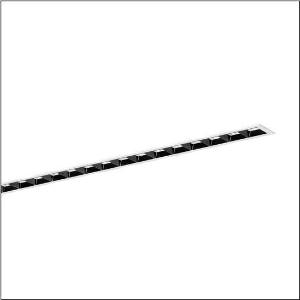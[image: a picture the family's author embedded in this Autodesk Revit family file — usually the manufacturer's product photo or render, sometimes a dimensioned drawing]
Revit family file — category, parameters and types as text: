
# Revit family: silica_r__21_51mx14dc4awb_d642
name_source: partatom
category: Lighting Fixtures
units: mm (PartAtom-declared; Revit-internal decimal feet)

## family parameters
Cut with Voids When Loaded = No
Host = Face
Light Source = No
Part Type = Normal
Room Calculation Point = No
Round Connector Dimension = Use Diameter
Shared = No

## types (1)
- --- (1 x LED, 10800 lm, 73.7 W, 4000K)
    Apparent Load = 74 VA
    CIE Flux Codes = 74 94 99 100 100
    Color Rendering = 80
    Color Temperature = 4000K
    Default Elevation = 1800 mm
    Description = Silica® 21, office luminaire, primary light control with darklight reflector, of PMMA, black, light emission: direct distribution, primary light characteristic: asymmetric, installation type: recessed, LED, rated luminous flux: 10.800lm, luminous efficacy: 147lm/W, light colour: 840, colour temperature: 4000K, with terminal, 3+2-pole, max. 2.5mm², mains connection: 220..240V, AC, 50/60Hz, rated input power: 73.7W, luminaire housing, of aluminium, traffic white (RAL 9016), length: 3.028mm, width: 79mm, height: 53mm, protection rating (complete): IP20, insulation class (complete): insulation class I (protective earthing), certification: CE, permissible operating ambient temperature: 0..+35°C, standard: EN 50419, packaging unit: 1 piece
    Height = 0 mm  [stored 0 ft]
    Lamp = 1 x LED
    Lamp Light Flux = 10800 lm
    Lamp Power = 73.7 W
    Lamp count = 1
    Length = 3027 mm
    Luminous efficacy = 147 lm/W
    Manufacturer = Siteco
    ModVariant = No
    Model = 51MX14DC4AWB
    Mounting Place = Ceiling
    Mounting Type = Recessed
    Number of Poles = 1
    OnlyDefault = Yes
    Power Factor = 1
    Product Name = Silica® 21
    Product group = office luminaire | ceiling recessed
    ProductGroupID = 401
    Protection Class = Protection class I
    Protection Degree = IP 20
    RLX_Detail_Level = 1
    RLX_Emergency_Light_Flux = 0 lm
    RLX_Emergency_Type = 0
    RLX_Emergency_Type_DB = No
    RlxData = <blob elided: 63137 chars, md5=51113b60>
    Socket = socket
    Standby Power = 0 W
    System Light Flux = 10800 lm
    System Power = 74 W
    Type Comments = factory setting: luminous flux: 100 % | dim-lin: 254 | 418 mA
    Type Image = l_1297791.jpg
    URL = http://relux.com
    VarID = @adj_053057
    Voltage = 0 V
    Weight = 0.00 kg
    Width = 79 mm

note: [stored X ft] marks values corroborated as IEEE doubles in the binary element streams (Revit-internal decimal feet)

## geometry (parser evidence)
native form markers: Blend x4, Sweep x11
no freeform markers — native parametric forms only
